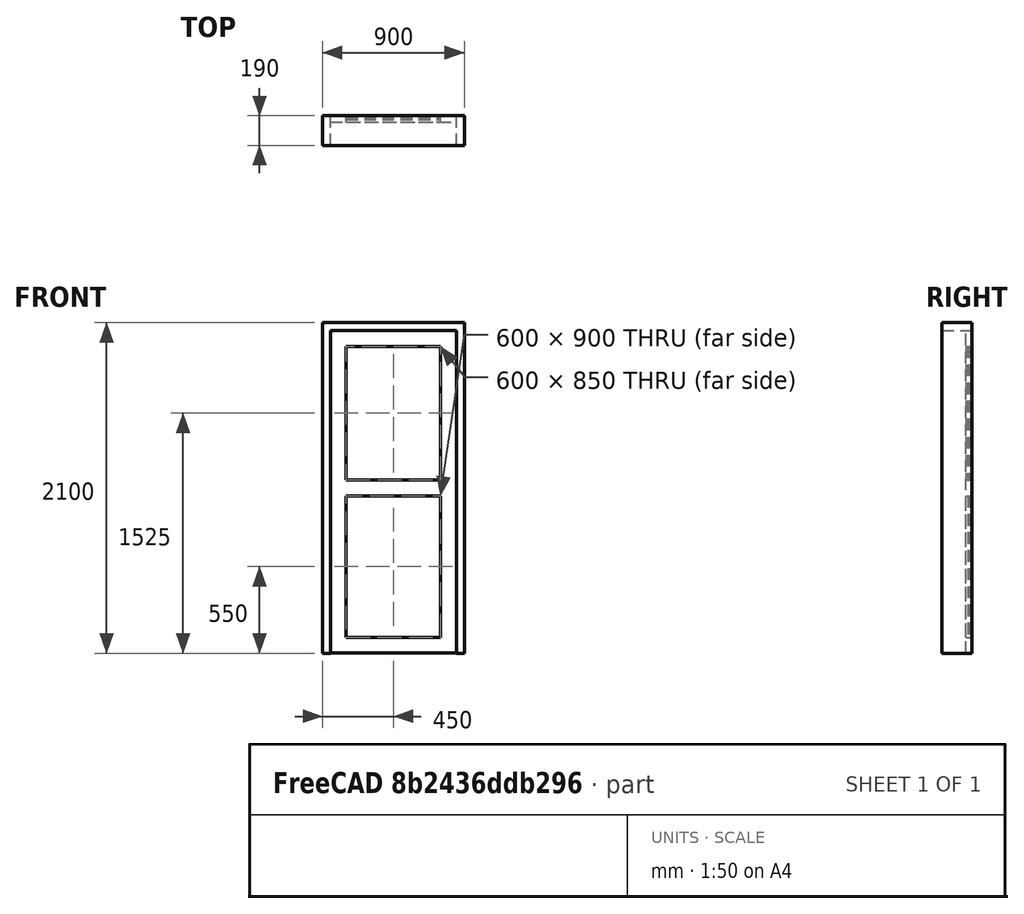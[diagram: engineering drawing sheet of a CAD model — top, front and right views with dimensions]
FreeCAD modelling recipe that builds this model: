
FCSTD DOCUMENT  (FreeCAD 0.16R6704 (Git))
Label: Simple door with glass
License: CreativeCommons Attribution
LicenseURL: http://creativecommons.org/licenses/by/4.0/
objects: Sketcher::SketchObject×1, Part::FeaturePython×1
note: 2 computed .brp shape members not serialized (recipe doc carries the construction recipe); baked Part::Feature solids carry a one-line shape summary decoded from their .brp

FEATURE [Sketcher::SketchObject] Sketch174  label="Sketch"
  Placement = pos=(0,0,0) rot=(1,0,0;1.5708rad)
  sketch-geometry (21):
    g0: LineSegment StartX=0 StartY=0 StartZ=0 EndX=900 EndY=0 EndZ=0
    g1: LineSegment StartX=900 StartY=0 StartZ=0 EndX=900 EndY=2100 EndZ=0
    g2: LineSegment StartX=900 StartY=2100 StartZ=0 EndX=0 EndY=2100 EndZ=0
    g3: LineSegment StartX=0 StartY=2100 StartZ=0 EndX=0 EndY=0 EndZ=0
    g4: LineSegment StartX=50 StartY=0 StartZ=0 EndX=850 EndY=0 EndZ=0
    g5: LineSegment StartX=850 StartY=0 StartZ=0 EndX=850 EndY=2050 EndZ=0
    g6: LineSegment StartX=850 StartY=2050 StartZ=0 EndX=50 EndY=2050 EndZ=0
    g7: LineSegment StartX=50 StartY=2050 StartZ=0 EndX=50 EndY=0 EndZ=0
    g8: LineSegment StartX=150 StartY=1950 StartZ=0 EndX=750 EndY=1950 EndZ=0
    g9: LineSegment StartX=750 StartY=1950 StartZ=0 EndX=750 EndY=1100 EndZ=0
    g10: LineSegment StartX=750 StartY=1100 StartZ=0 EndX=150 EndY=1100 EndZ=0
    g11: LineSegment StartX=150 StartY=1100 StartZ=0 EndX=150 EndY=1950 EndZ=0
    g12: LineSegment StartX=150 StartY=1000 StartZ=0 EndX=750 EndY=1000 EndZ=0
    g13: LineSegment StartX=750 StartY=1000 StartZ=0 EndX=750 EndY=100 EndZ=0
    g14: LineSegment StartX=750 StartY=100 StartZ=0 EndX=150 EndY=100 EndZ=0
    g15: LineSegment StartX=150 StartY=100 StartZ=0 EndX=150 EndY=1000 EndZ=0
    g16: LineSegment [constr] StartX=-278 StartY=1050 StartZ=0 EndX=1352 EndY=1050 EndZ=0
    g17: LineSegment StartX=51 StartY=2049 StartZ=0 EndX=849 EndY=2049 EndZ=0
    g18: LineSegment StartX=849 StartY=2049 StartZ=0 EndX=849 EndY=1 EndZ=0
    g19: LineSegment StartX=849 StartY=1 StartZ=0 EndX=51 EndY=1 EndZ=0
    g20: LineSegment StartX=51 StartY=1 StartZ=0 EndX=51 EndY=2049 EndZ=0
  constraints (61):
    c: Coincident(g0,g1)
    c: Coincident(g1,g2)
    c: Coincident(g2,g3)
    c: Coincident(g3,g0)
    c: Horizontal(g0)
    c: Horizontal(g2)
    c: Vertical(g1)
    c: Vertical(g3)
    c: Coincident(g4,g5)
    c: Coincident(g5,g6)
    c: Coincident(g6,g7)
    c: Coincident(g7,g4)
    c: Horizontal(g4)
    c: Horizontal(g6)
    c: Vertical(g5)
    c: Vertical(g7)
    c: DistanceY(g1) = 2100  'Altura da vão'
    c: DistanceX(g0) = 900  'Largura do vão'
    c: DistanceY(g6,g2) = 50  'Altura batente'
    c: DistanceX(g2,g6) = 50  'Batente vertical 1'
    c: DistanceX(g4,g0) = 50  'Montante vertical 2'
    c: DistanceY(g0,g4) = 0
    c: Coincident(g0,g-1)
    c: Coincident(g8,g9)
    c: Coincident(g9,g10)
    c: Coincident(g10,g11)
    c: Coincident(g11,g8)
    c: Horizontal(g8)
    c: Horizontal(g10)
    c: Vertical(g9)
    c: Vertical(g11)
    c: Coincident(g12,g13)
    c: Coincident(g13,g14)
    c: Coincident(g14,g15)
    c: Coincident(g15,g12)
    c: Horizontal(g12)
    c: Horizontal(g14)
    c: Vertical(g13)
    c: Vertical(g15)
    c: DistanceX(g10,g12) = 0
    c: DistanceX(g9,g12) = 0
    c: DistanceY(g12,g10) = 100  'Montante intermediário'
    c: DistanceY(g8,g6) = 100  'Montante superior'
    c: DistanceX(g6,g8) = 100  'Montante porta vertical 1'
    c: DistanceX(g8,g5) = 100  'Montante vertical 2 porta'
    c: DistanceY(g-1,g14) = 100  'Altura do montante inferior porta'
    c: Horizontal(g16)
    c: Symmetric(g10,g12,g16)
    c: DistanceY(g-1,g16) = 1050  'Altura moldura intermediário porta ao chão'
    c: Coincident(g17,g18)
    c: Coincident(g18,g19)
    c: Coincident(g19,g20)
    c: Coincident(g20,g17)
    c: Horizontal(g17)
    c: Horizontal(g19)
    c: Vertical(g18)
    c: Vertical(g20)
    c: DistanceX(g18,g4) = 1
    c: DistanceY(g4,g18) = 1
    c: DistanceX(g6,g17) = 1
    c: DistanceY(g17,g6) = 1
FEATURE [Part::FeaturePython] Window107  label="Simple door with glass"  # WARN: FeaturePython — macro-defined, semantics opaque (R4)
  Base = -> Sketch174
  Height = 2100
  HoleDepth = 0
  MoveWithHost = true
  Normal = (0,1,0)
  Preset = 6
  Role = 1
  Width = 900
  WindowParts = BATENTE | Frame | Wire0,Wire1 | 190.0 | 0.0 | PORTA | Frame | Wire2,Wire3,Wire4 | 40.0 | 150.0 | VIDRO SUPERIOR | Glass panel | Wire2 | 10.0 | 165.0 | VIDRO INFERIOR | Glass panel | Wire3 | 10.0 | 165.0
